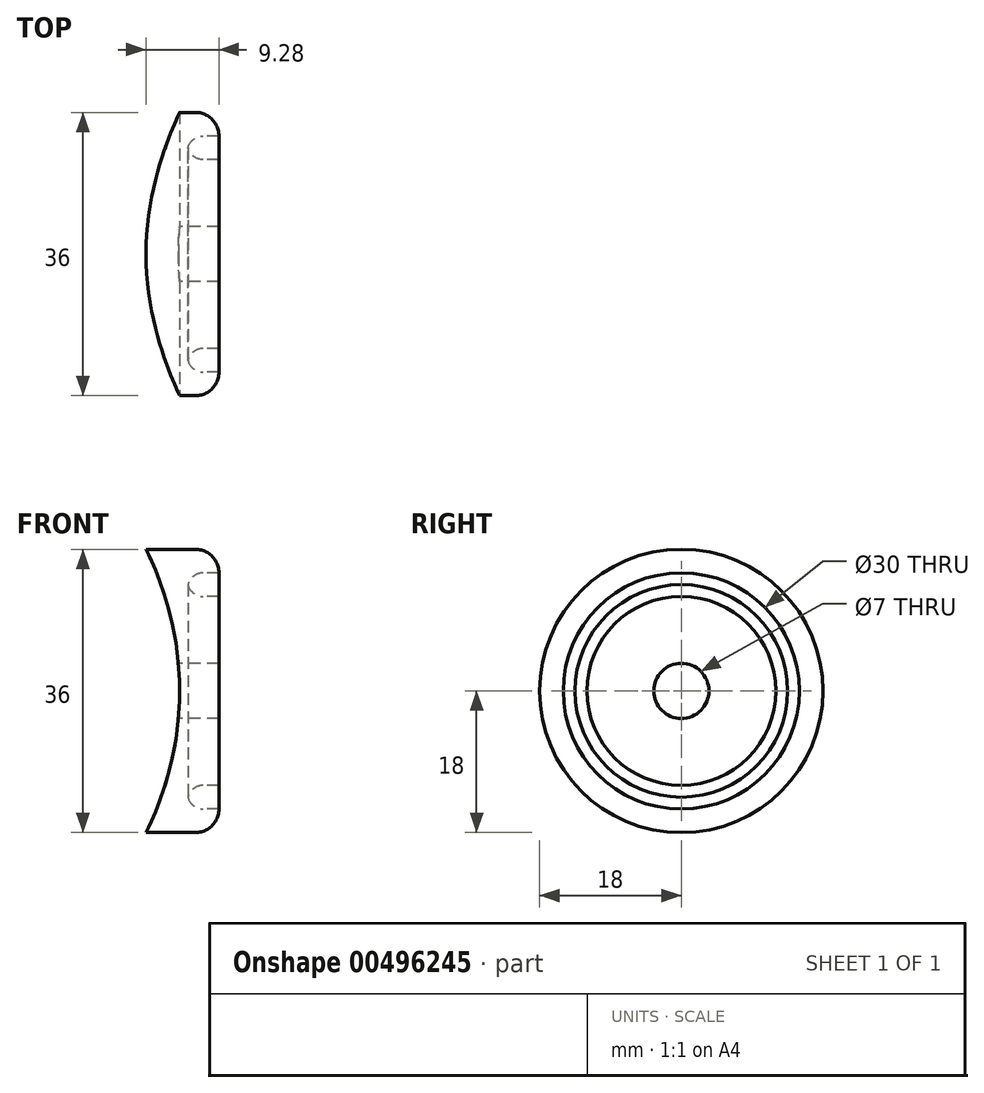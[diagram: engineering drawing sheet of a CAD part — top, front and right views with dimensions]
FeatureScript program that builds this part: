
annotation { "Feature Type Name" : "Feature", "Feature Type Description" : "" }
export const myFeature = defineFeature(function(context is Context, id is Id, definition is map)
    precondition{}
    {
        {
            var Q0;
            Q0=qCreatedBy(makeId("Front.planeOp"),FACE);
            var sketch = newSketch(context, id + "F0", { "sketchPlane" : qUnion([Q0])});
            skLineSegment(sketch, "E0", {"start": v(-29.6, 18) * mm, "end": v(6.34, 18) * mm});
            skLineSegment(sketch, "E1", {"start": v(9.34, 15) * mm, "end": v(9.34, 15) * mm});
            skLineSegment(sketch, "E2", {"start": v(9.34, 15) * mm, "end": v(7.34, 15) * mm});
            skLineSegment(sketch, "E3", {"start": v(5.34, 14) * mm, "end": v(5.34, 13) * mm});
            skLineSegment(sketch, "E4", {"start": v(7.34, 12) * mm, "end": v(9.34, 12) * mm});
            skLineSegment(sketch, "E5", {"start": v(9.34, 12) * mm, "end": v(9.34, 0) * mm});
            skLineSegment(sketch, "E6", {"start": v(-63.34, 0) * mm, "end": v(57.12, 0) * mm, "construction": true});
            skLineSegment(sketch, "E7", {"start": v(9.34, 3.5) * mm, "end": v(-15.77, 3.5) * mm});
            skLineSegment(sketch, "E8", {"start": v(-29.6, 18) * mm, "end": v(-29.6, 3.5) * mm});
            skLineSegment(sketch, "E9", {"start": v(-15.77, 3.5) * mm, "end": v(-29.6, 3.5) * mm});
            skPoint(sketch, "E10.visualSharp", {"position": v(9.34, 18) * mm});
            skArc(sketch, "E10.filletArc", {"start": v(9.34, 15) * mm, "mid": v(8.46, 17.12) * mm, "end": v(6.34, 18) * mm});
            skPoint(sketch, "E11.visualSharp", {"position": v(5.34, 15) * mm});
            skArc(sketch, "E11.filletArc", {"start": v(7.34, 15) * mm, "mid": v(5.92, 14.41) * mm, "end": v(5.34, 13) * mm});
            skPoint(sketch, "E12.visualSharp", {"position": v(5.34, 12) * mm});
            skArc(sketch, "E12.filletArc", {"start": v(5.34, 14) * mm, "mid": v(5.92, 12.59) * mm, "end": v(7.34, 12) * mm});
            skLineSegment(sketch, "E13", {"start": v(3.84, 30.97) * mm, "end": v(3.84, -37.3) * mm, "construction": true});
            skPoint(sketch, "E14", {"position": v(3.84, 0) * mm});
            skSolve(sketch);
        }
        {
            var Q0;
            {var subQ0=sQuery(id+"F0.wireOp",EDGE,"E3");Q0=makeQuery(id+"F0.imprint","IMPRINT",FACE,{"disambiguationData":[TD([[makeQuery(id+"F0.imprint","IMPRINT",EDGE,{"derivedFrom":subQ0}),1.0]])]});}
            var Q1;
            Q1=makeQuery(id+"F0.imprint","IMPRINT",FACE,{"disambiguationData":[TD([[makeQuery(id+"F0.imprint","IMPRINT",EDGE,{"derivedFrom":sQuery(id+"F0.wireOp",EDGE,"E0")}),-1.0]])]});
            var Q2;
            {var subQ0=sQuery(id+"F0.wireOp",EDGE,"E3");Q2=makeQuery(id+"F0.imprint","IMPRINT",FACE,{"disambiguationData":[TD([[makeQuery(id+"F0.imprint","IMPRINT",EDGE,{"derivedFrom":subQ0}),1.0]])]});}
            var Q3;
            Q3=sQuery(id+"F0.wireOp",EDGE,"E6");
            revolve(context, id + "F1", {"entities" : qUnion([Q0, Q1, Q2]), "axis" : qUnion([Q3]), "revolveType" : RevolveType.FULL});
        }
        {
            var Q0;
            Q0=qCreatedBy(makeId("Front.planeOp"),FACE);
            var sketch = newSketch(context, id + "F2", { "sketchPlane" : qUnion([Q0])});
            skLineSegment(sketch, "E15", {"start": v(4.34, 23.46) * mm, "end": v(4.34, -24.31) * mm, "construction": true});
            skLineSegment(sketch, "E16", {"start": v(-35.66, 3.26) * mm, "end": v(-35.66, -4.89) * mm, "construction": true});
            skLineSegment(sketch, "E17", {"start": v(-39.6, 0) * mm, "end": v(-32.63, 0) * mm, "construction": true});
            skPoint(sketch, "E18", {"position": v(-35.66, 0) * mm});
            skCircle(sketch, "E19", {"center": v(-35.66, 0) * mm, "radius": 40 * mm});
            skSolve(sketch);
        }
        {
            var Q0;
            Q0 = qSketchRegion(id + "F2", true);
            extrude(context, id + "F3", {"entities" : qUnion([Q0]), "operationType" : NewBodyOperationType.REMOVE, "endBound" : BoundingType.SYMMETRIC, "oppositeDirection" : true, "depth" : 35 * mm});
        }
        {
            var Q0;
            Q0 = qSketchRegion(id + "F2", true);
            extrude(context, id + "F4", {"entities" : qUnion([Q0]), "operationType" : NewBodyOperationType.ADD, "endBound" : BoundingType.SYMMETRIC, "depth" : 66 * mm});
        }
        {
            var Q0;
            Q0=makeQuery(id+"F4.opExtrude","CAP_FACE",FACE,{"disambiguationData":[OSD([sQuery(id+"F2.wireOp",EDGE,"E19")])],"isStart":false});
            extrude(context, id + "F5", {"entities" : qUnion([Q0]), "operationType" : NewBodyOperationType.REMOVE, "oppositeDirection" : true, "depth" : 80 * mm});
        }
    });
